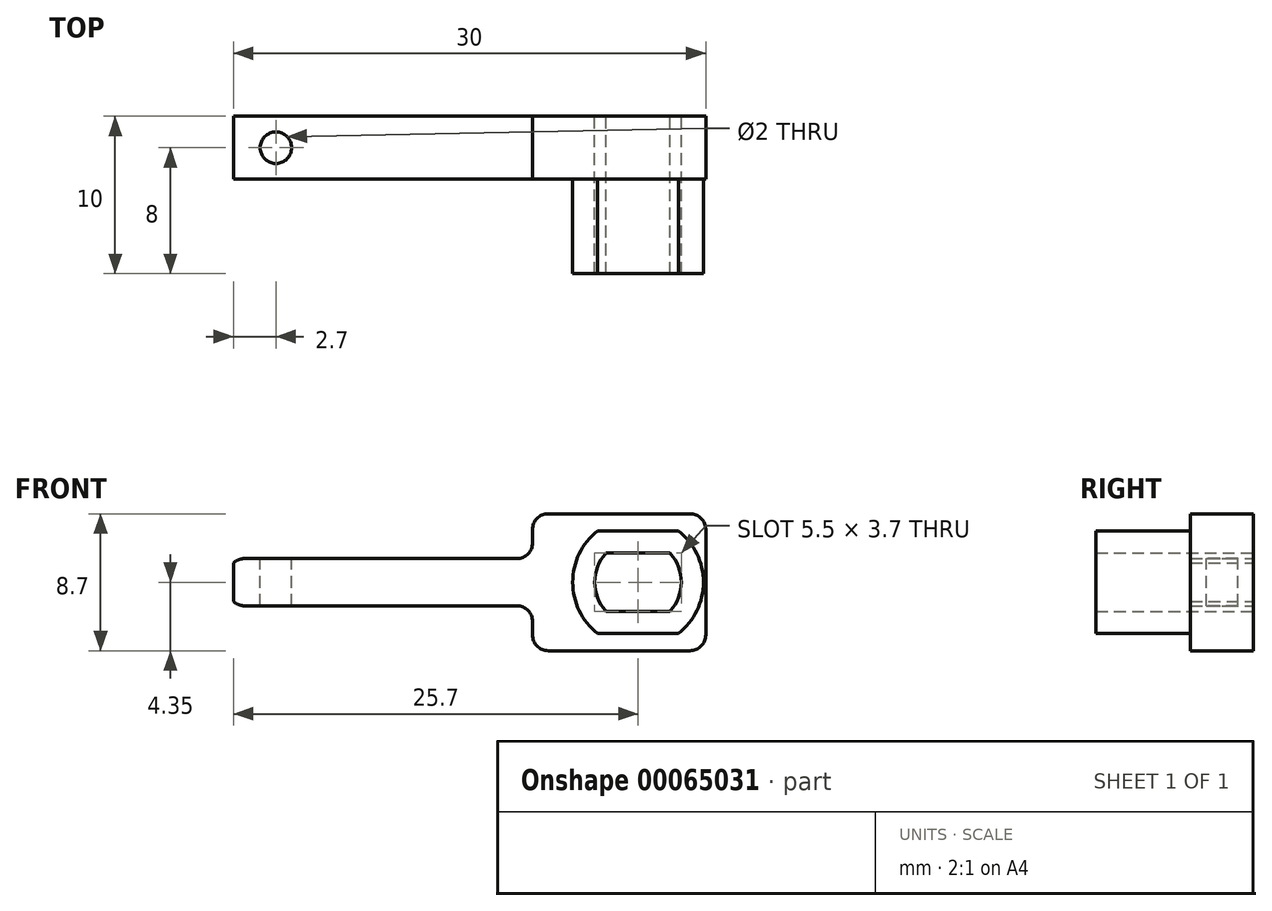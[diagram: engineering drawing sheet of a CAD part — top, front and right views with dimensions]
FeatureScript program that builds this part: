
annotation { "Feature Type Name" : "Feature", "Feature Type Description" : "" }
export const myFeature = defineFeature(function(context is Context, id is Id, definition is map)
    precondition{}
    {
        {
            var Q0;
            Q0=qCreatedBy(makeId("Front.planeOp"),FACE);
            var sketch = newSketch(context, id + "F0", { "sketchPlane" : qUnion([Q0])});
            skArc(sketch, "E0", {"start": v(-2.03, 1.85) * mm, "mid": v(-2.75, 0) * mm, "end": v(-2.03, -1.85) * mm});
            skLineSegment(sketch, "E1.bottom", {"start": v(4.3, 4.35) * mm, "end": v(-5.7, 4.35) * mm});
            skLineSegment(sketch, "E1.left", {"start": v(4.3, 4.35) * mm, "end": v(4.3, 0) * mm});
            skLineSegment(sketch, "E2", {"start": v(4.3, 0) * mm, "end": v(4.3, -4.35) * mm});
            skLineSegment(sketch, "E3", {"start": v(-2.03, 1.85) * mm, "end": v(2.03, 1.85) * mm});
            skLineSegment(sketch, "E4", {"start": v(-2.03, -1.85) * mm, "end": v(2.03, -1.85) * mm});
            skArc(sketch, "E5.trimOffspring", {"start": v(2.03, -1.85) * mm, "mid": v(2.75, 0) * mm, "end": v(2.03, 1.85) * mm});
            skPoint(sketch, "E6.firstSnap0", {"position": v(-2.75, 0) * mm});
            skLineSegment(sketch, "E7", {"start": v(-6.7, 3.35) * mm, "end": v(-6.7, 2.5) * mm});
            skArc(sketch, "E8.filletArc", {"start": v(-5.7, 4.35) * mm, "mid": v(-6.4, 4.06) * mm, "end": v(-6.7, 3.35) * mm});
            skPoint(sketch, "E9.visualSharp", {"position": v(-6.7, 1.78) * mm});
            skArc(sketch, "E9.filletArc", {"start": v(-7.7, 1.5) * mm, "mid": v(-7, 1.8) * mm, "end": v(-6.7, 2.5) * mm});
            skLineSegment(sketch, "E10", {"start": v(-25, 1.5) * mm, "end": v(-7.7, 1.5) * mm});
            skPoint(sketch, "E11.visualSharp", {"position": v(-26, 1.5) * mm});
            skArc(sketch, "E11.filletArc", {"start": v(-25, 1.5) * mm, "mid": v(-25.38, 1.43) * mm, "end": v(-25.7, 1.21) * mm});
            skLineSegment(sketch, "E12", {"start": v(0, 0) * mm, "end": v(4.3, 0) * mm, "construction": true});
            skLineSegment(sketch, "E13.MirrorCS", {"start": v(4.3, -4.35) * mm, "end": v(-5.7, -4.35) * mm});
            skLineSegment(sketch, "E14.MirrorCS", {"start": v(-25, -1.5) * mm, "end": v(-7.7, -1.5) * mm});
            skLineSegment(sketch, "E15.MirrorCS", {"start": v(-6.7, -3.35) * mm, "end": v(-6.7, -2.5) * mm});
            skArc(sketch, "E16.MirrorCS", {"start": v(-25, -1.5) * mm, "mid": v(-25.38, -1.43) * mm, "end": v(-25.7, -1.21) * mm});
            skArc(sketch, "E17.MirrorCS", {"start": v(-7.7, -1.5) * mm, "mid": v(-7, -1.8) * mm, "end": v(-6.7, -2.5) * mm});
            skPoint(sketch, "E18.MirrorP", {"position": v(-26, -1.5) * mm});
            skPoint(sketch, "E19.MirrorP", {"position": v(-6.7, -1.78) * mm});
            skArc(sketch, "E20.MirrorCS", {"start": v(-5.7, -4.35) * mm, "mid": v(-6.4, -4.06) * mm, "end": v(-6.7, -3.35) * mm});
            skLineSegment(sketch, "E21", {"start": v(-25.7, 1.21) * mm, "end": v(-25.7, -1.21) * mm});
            skSolve(sketch);
        }
        {
            var Q0;
            Q0 = qSketchRegion(id + "F0", true);
            extrude(context, id + "F1", {"entities" : qUnion([Q0]), "depth" : 4 * mm});
        }
        {
            var Q0;
            Q0=makeQuery(id+"F1.opExtrude","SWEPT_FACE",FACE,{"disambiguationData":[OSD([sQuery(id+"F0.wireOp",EDGE,"E1.bottom")])]});
            var sketch = newSketch(context, id + "F2", { "sketchPlane" : qUnion([Q0])});
            skLineSegment(sketch, "E22", {"start": v(-23, 0) * mm, "end": v(-23, -4) * mm, "construction": true});
            skCircle(sketch, "E23", {"center": v(-23, -2) * mm, "radius": 1.33 * mm});
            skSolve(sketch);
        }
        {
            var Q0;
            Q0=sQuery(id+"F2.wireOp",VERTEX,"E23.center");
            var Q1;
            Q1=makeQuery(id+"F1.opExtrude","SWEPT_BODY",BODY,{"disambiguationData":[OSD([sQuery(id+"F0.wireOp",EDGE,"E0"),sQuery(id+"F0.wireOp",EDGE,"E1.bottom"),sQuery(id+"F0.wireOp",EDGE,"E1.top"),sQuery(id+"F0.wireOp",EDGE,"E1.left"),sQuery(id+"F0.wireOp",EDGE,"E1.right"),sQuery(id+"F0.wireOp",EDGE,"E2"),sQuery(id+"F0.wireOp",EDGE,"E3"),sQuery(id+"F0.wireOp",EDGE,"E4"),sQuery(id+"F0.wireOp",EDGE,"E5.trimOffspring")])]});
            hole(context, id + "F3", {"style" : HoleStyle.SIMPLE, "holeDiameter" : 2 * mm, "endStyle" : HoleEndStyle.THROUGH, "locations" : qUnion([Q0]), "scope" : qUnion([Q1])});
        }
        {
            var Q0;
            Q0=makeQuery(id+"F1.opExtrude","SWEPT_EDGE",EDGE,{"disambiguationData":[OSD([sQuery(id+"F0.wireOp",EDGE,"E1.bottom"),sQuery(id+"F0.wireOp",EDGE,"E1.left")])]});
            fillet(context, id + "F4", {"entities" : qUnion([Q0]), "radius" : 1 * mm, "tangentPropagation" : true, "allowEdgeOverflow" : false});
        }
        {
            var Q0;
            Q0=makeQuery(id+"F1.opExtrude","SWEPT_EDGE",EDGE,{"disambiguationData":[OSD([sQuery(id+"F0.wireOp",EDGE,"E2"),sQuery(id+"F0.wireOp",EDGE,"E13.MirrorCS")])]});
            fillet(context, id + "F5", {"entities" : qUnion([Q0]), "radius" : 1 * mm, "tangentPropagation" : true, "allowEdgeOverflow" : false});
        }
        {
            var Q0;
            Q0=makeQuery(id+"F1.opExtrude","CAP_FACE",FACE,{"disambiguationData":[OSD([sQuery(id+"F0.wireOp",EDGE,"E0"),sQuery(id+"F0.wireOp",EDGE,"E1.bottom"),sQuery(id+"F0.wireOp",EDGE,"E1.left"),sQuery(id+"F0.wireOp",EDGE,"E2"),sQuery(id+"F0.wireOp",EDGE,"E3"),sQuery(id+"F0.wireOp",EDGE,"E4"),sQuery(id+"F0.wireOp",EDGE,"E5.trimOffspring"),sQuery(id+"F0.wireOp",EDGE,"E7"),sQuery(id+"F0.wireOp",EDGE,"E8.filletArc"),sQuery(id+"F0.wireOp",EDGE,"E9.filletArc"),sQuery(id+"F0.wireOp",EDGE,"E10"),sQuery(id+"F0.wireOp",EDGE,"E11.filletArc"),sQuery(id+"F0.wireOp",EDGE,"E13.MirrorCS"),sQuery(id+"F0.wireOp",EDGE,"E14.MirrorCS"),sQuery(id+"F0.wireOp",EDGE,"E15.MirrorCS"),sQuery(id+"F0.wireOp",EDGE,"E16.MirrorCS"),sQuery(id+"F0.wireOp",EDGE,"E17.MirrorCS"),sQuery(id+"F0.wireOp",EDGE,"E20.MirrorCS"),sQuery(id+"F0.wireOp",EDGE,"E21")])],"isStart":false});
            var sketch = newSketch(context, id + "F6", { "sketchPlane" : qUnion([Q0])});
            skLineSegment(sketch, "E24.0", {"start": v(-2.58, -3.25) * mm, "end": v(2.58, -3.25) * mm});
            skArc(sketch, "E24.1", {"start": v(-2.58, 3.25) * mm, "mid": v(-4.15, 0) * mm, "end": v(-2.58, -3.25) * mm});
            skLineSegment(sketch, "E24.2", {"start": v(-2.58, 3.25) * mm, "end": v(2.58, 3.25) * mm});
            skArc(sketch, "E24.3", {"start": v(2.58, -3.25) * mm, "mid": v(4.15, 0) * mm, "end": v(2.58, 3.25) * mm});
            skSolve(sketch);
        }
        {
            var Q0;
            Q0=makeQuery(id+"F6.imprint","IMPRINT",FACE,{"disambiguationData":[TD([[makeQuery(id+"F6.imprint","IMPRINT",EDGE,{"derivedFrom":sQuery(id+"F6.wireOp",EDGE,"E24.0")}),1.0]])]});
            extrude(context, id + "F7", {"entities" : qUnion([Q0]), "operationType" : NewBodyOperationType.ADD, "depth" : 6 * mm});
        }
    });
